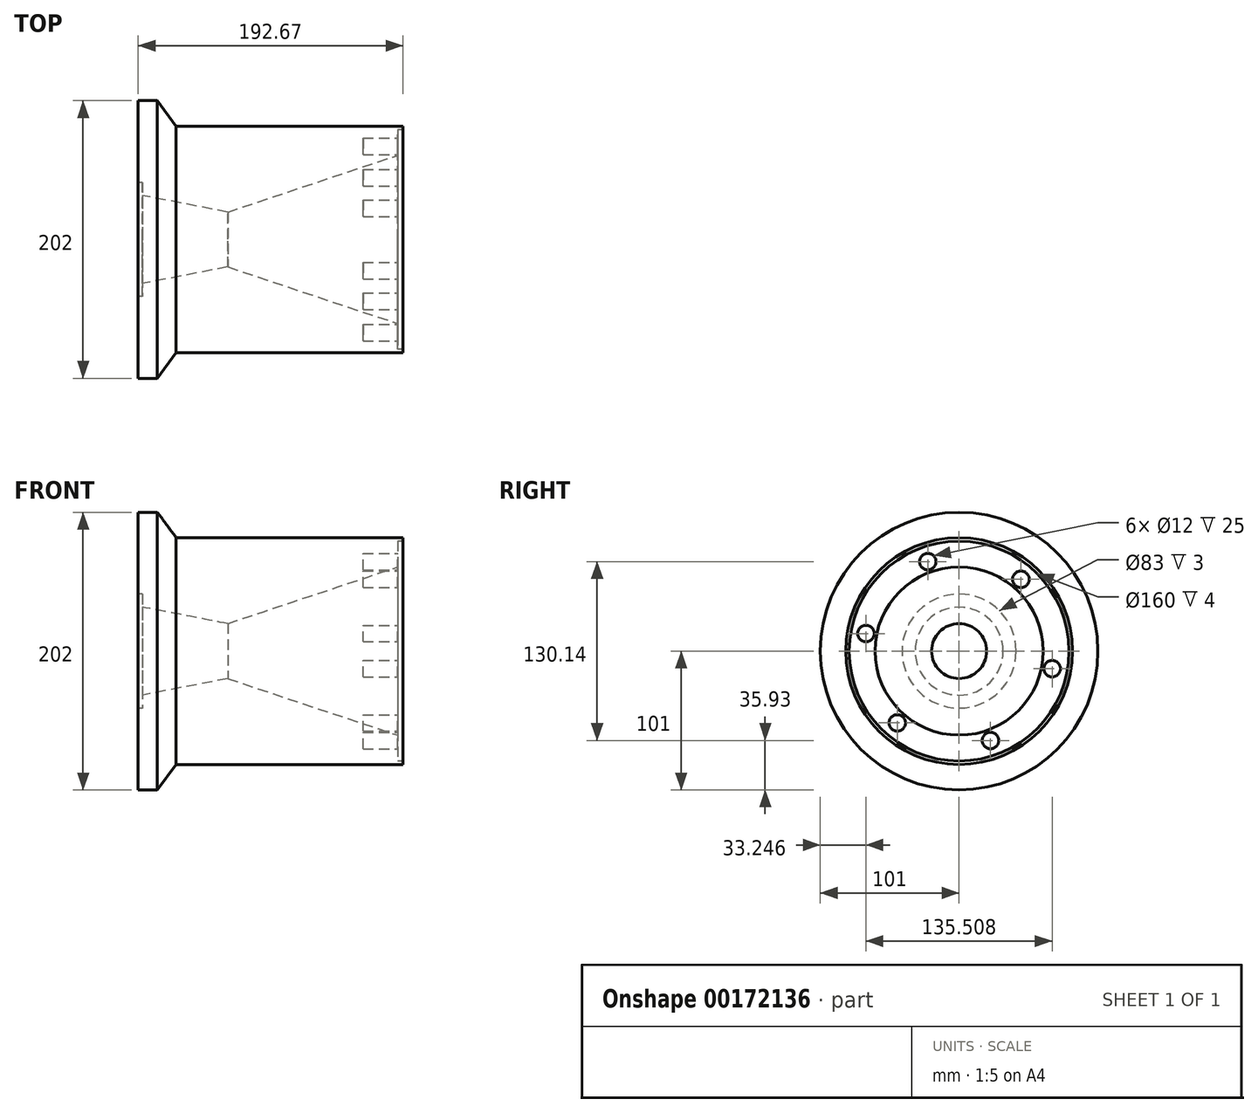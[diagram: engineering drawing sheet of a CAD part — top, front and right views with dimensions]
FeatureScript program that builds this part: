
annotation { "Feature Type Name" : "Feature", "Feature Type Description" : "" }
export const myFeature = defineFeature(function(context is Context, id is Id, definition is map)
    precondition{}
    {
        {
            var Q0;
            Q0=qCreatedBy(makeId("Front.planeOp"),FACE);
            var sketch = newSketch(context, id + "F0", { "sketchPlane" : qUnion([Q0])});
            skLineSegment(sketch, "E0", {"start": v(-80.55, 124) * mm, "end": v(-80.55, 183.5) * mm});
            skLineSegment(sketch, "E1", {"start": v(-80.55, 183.5) * mm, "end": v(-66.55, 183.5) * mm});
            skLineSegment(sketch, "E2", {"start": v(-66.55, 183.5) * mm, "end": v(-52.88, 165) * mm});
            skLineSegment(sketch, "E3", {"start": v(-52.88, 165) * mm, "end": v(-37.88, 165) * mm});
            skLineSegment(sketch, "E4", {"start": v(112.12, 162.5) * mm, "end": v(112.12, 165) * mm});
            skLineSegment(sketch, "E5", {"start": v(112.12, 165) * mm, "end": v(-37.88, 165) * mm});
            skPoint(sketch, "E6.endSnap0", {"position": v(-80.55, 82.5) * mm});
            skLineSegment(sketch, "E7", {"start": v(-261.09, 82.5) * mm, "end": v(-80.55, 82.5) * mm});
            skLineSegment(sketch, "E8", {"start": v(-80.55, 124) * mm, "end": v(-77.55, 124) * mm});
            skLineSegment(sketch, "E9", {"start": v(-77.55, 124) * mm, "end": v(-77.55, 114.5) * mm});
            skLineSegment(sketch, "E10", {"start": v(-77.55, 114.5) * mm, "end": v(-15.38, 102.5) * mm});
            skLineSegment(sketch, "E11", {"start": v(-15.38, 102.5) * mm, "end": v(108.12, 143.67) * mm});
            skPoint(sketch, "E12.orphan", {"position": v(112.12, 82.5) * mm});
            skLineSegment(sketch, "E13.trimOffspring", {"start": v(112.12, 82.5) * mm, "end": v(310.1, 82.5) * mm});
            skLineSegment(sketch, "E14", {"start": v(112.12, 162.5) * mm, "end": v(108.12, 162.5) * mm});
            skLineSegment(sketch, "E15", {"start": v(108.12, 162.5) * mm, "end": v(108.12, 143.67) * mm});
            skPoint(sketch, "E16.orphan", {"position": v(112.12, 145) * mm});
            skSolve(sketch);
        }
        {
            var Q0;
            Q0=makeQuery(id+"F0.imprint","IMPRINT",FACE,{"disambiguationData":[TD([[makeQuery(id+"F0.imprint","IMPRINT",EDGE,{"derivedFrom":sQuery(id+"F0.wireOp",EDGE,"E1")}),-1.0]])]});
            var Q1;
            Q1=sQuery(id+"F0.wireOp",EDGE,"E13.trimOffspring");
            revolve(context, id + "F1", {"entities" : qUnion([Q0]), "axis" : qUnion([Q1]), "revolveType" : RevolveType.ONE_DIRECTION, "angle" : 360 * degree});
        }
        {
            var Q0;
            Q0=makeQuery(id+"F1.opRevolve","SWEPT_FACE",FACE,{"disambiguationData":[OSD([sQuery(id+"F0.wireOp",EDGE,"E15")])]});
            var sketch = newSketch(context, id + "F2", { "sketchPlane" : qUnion([Q0])});
            skSolve(sketch);
        }
        {
            var Q0;
            {var subQ0=sQuery(id+"F0.wireOp",EDGE,"E15");Q0=makeQuery(id+"F2.imprint","IMPRINT",FACE,{"disambiguationData":[TD([[makeQuery(id+"F2.imprint","IMPRINT",EDGE,{"derivedFrom":makeQuery(id+"F1.opRevolve","SWEPT_EDGE",EDGE,{"disambiguationData":[OSD([sQuery(id+"F0.wireOp",EDGE,"E11"),subQ0])]})}),1.0]])]});}
            var sketch = newSketch(context, id + "F3", { "sketchPlane" : qUnion([Q0])});
            skCircle(sketch, "E17", {"center": v(-22.8, 147.57) * mm, "radius": 6 * mm});
            skPoint(sketch, "E18.second.point", {"position": v(19.22, 16.28) * mm});
            skPoint(sketch, "E18.third.point", {"position": v(-56.7, 43.27) * mm});
            skCircle(sketch, "E19.1.0", {"center": v(-67.75, 95.29) * mm, "radius": 6 * mm});
            skCircle(sketch, "E19.2.0", {"center": v(-44.95, 30.22) * mm, "radius": 6 * mm});
            skCircle(sketch, "E19.3.0", {"center": v(22.8, 17.43) * mm, "radius": 6 * mm});
            skCircle(sketch, "E19.4.0", {"center": v(67.75, 69.71) * mm, "radius": 6 * mm});
            skCircle(sketch, "E19.5.0", {"center": v(44.95, 134.78) * mm, "radius": 6 * mm});
            skPoint(sketch, "E19.center", {"position": v(0, 82.5) * mm});
            skArc(sketch, "E20.trimOffspring", {"start": v(17.06, 15.7) * mm, "mid": v(18.14, 15.98) * mm, "end": v(19.22, 16.28) * mm});
            skSolve(sketch);
        }
        {
            var Q0;
            Q0 = qSketchRegion(id + "F3", true);
            extrude(context, id + "F4", {"entities" : qUnion([Q0]), "operationType" : NewBodyOperationType.REMOVE, "oppositeDirection" : true, "depth" : 25 * mm});
        }
    });
